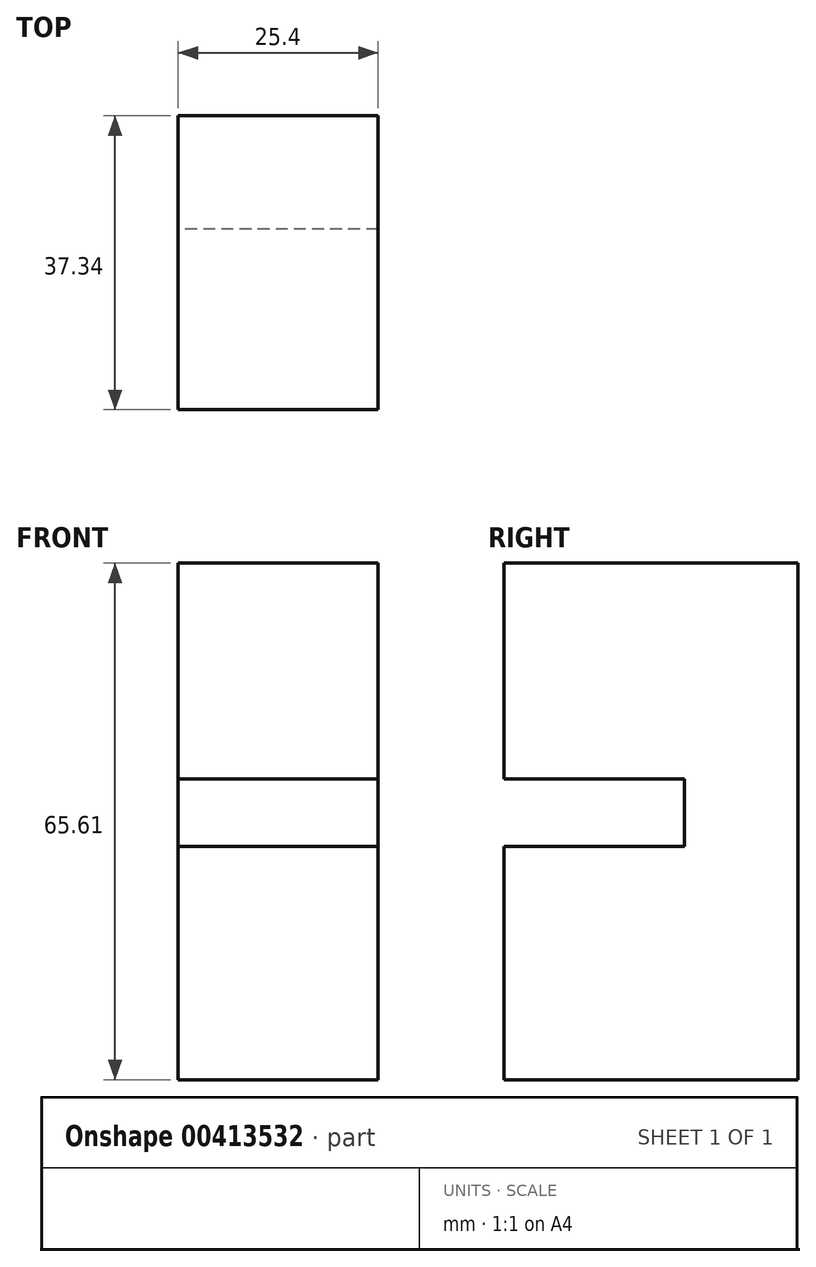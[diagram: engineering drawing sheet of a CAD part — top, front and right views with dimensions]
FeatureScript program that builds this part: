
annotation { "Feature Type Name" : "Feature", "Feature Type Description" : "" }
export const myFeature = defineFeature(function(context is Context, id is Id, definition is map)
    precondition{}
    {
        {
            var Q0;
            Q0=qCreatedBy(makeId("Right.planeOp"),FACE);
            var sketch = newSketch(context, id + "F0", { "sketchPlane" : qUnion([Q0])});
            skLineSegment(sketch, "E0.bottom", {"start": v(-37.34, 0) * mm, "end": v(0, 0) * mm});
            skLineSegment(sketch, "E0.top", {"start": v(-37.34, -65.6) * mm, "end": v(0, -65.6) * mm});
            skLineSegment(sketch, "E0.left", {"start": v(-37.34, 0) * mm, "end": v(-37.34, -65.6) * mm});
            skLineSegment(sketch, "E0.right", {"start": v(0, 0) * mm, "end": v(0, -65.6) * mm});
            skLineSegment(sketch, "E1.bottom", {"start": v(-72.37, -27.42) * mm, "end": v(-14.42, -27.42) * mm});
            skLineSegment(sketch, "E1.top", {"start": v(-72.37, -35.98) * mm, "end": v(-14.42, -35.98) * mm});
            skLineSegment(sketch, "E1.left", {"start": v(-72.37, -27.42) * mm, "end": v(-72.37, -35.98) * mm});
            skLineSegment(sketch, "E1.right", {"start": v(-14.42, -27.42) * mm, "end": v(-14.42, -35.98) * mm});
            skSolve(sketch);
        }
        {
            var Q0;
            {var subQ4=sQuery(id+"F0.wireOp",EDGE,"E0.bottom");Q0=makeQuery(id+"F0.imprint","IMPRINT",FACE,{"disambiguationData":[TD([[makeQuery(id+"F0.imprint","IMPRINT",EDGE,{"derivedFrom":subQ4}),-1.0]])]});}
            extrude(context, id + "F1", {"entities" : qUnion([Q0]), "depth" : 25.4 * mm});
        }
    });
